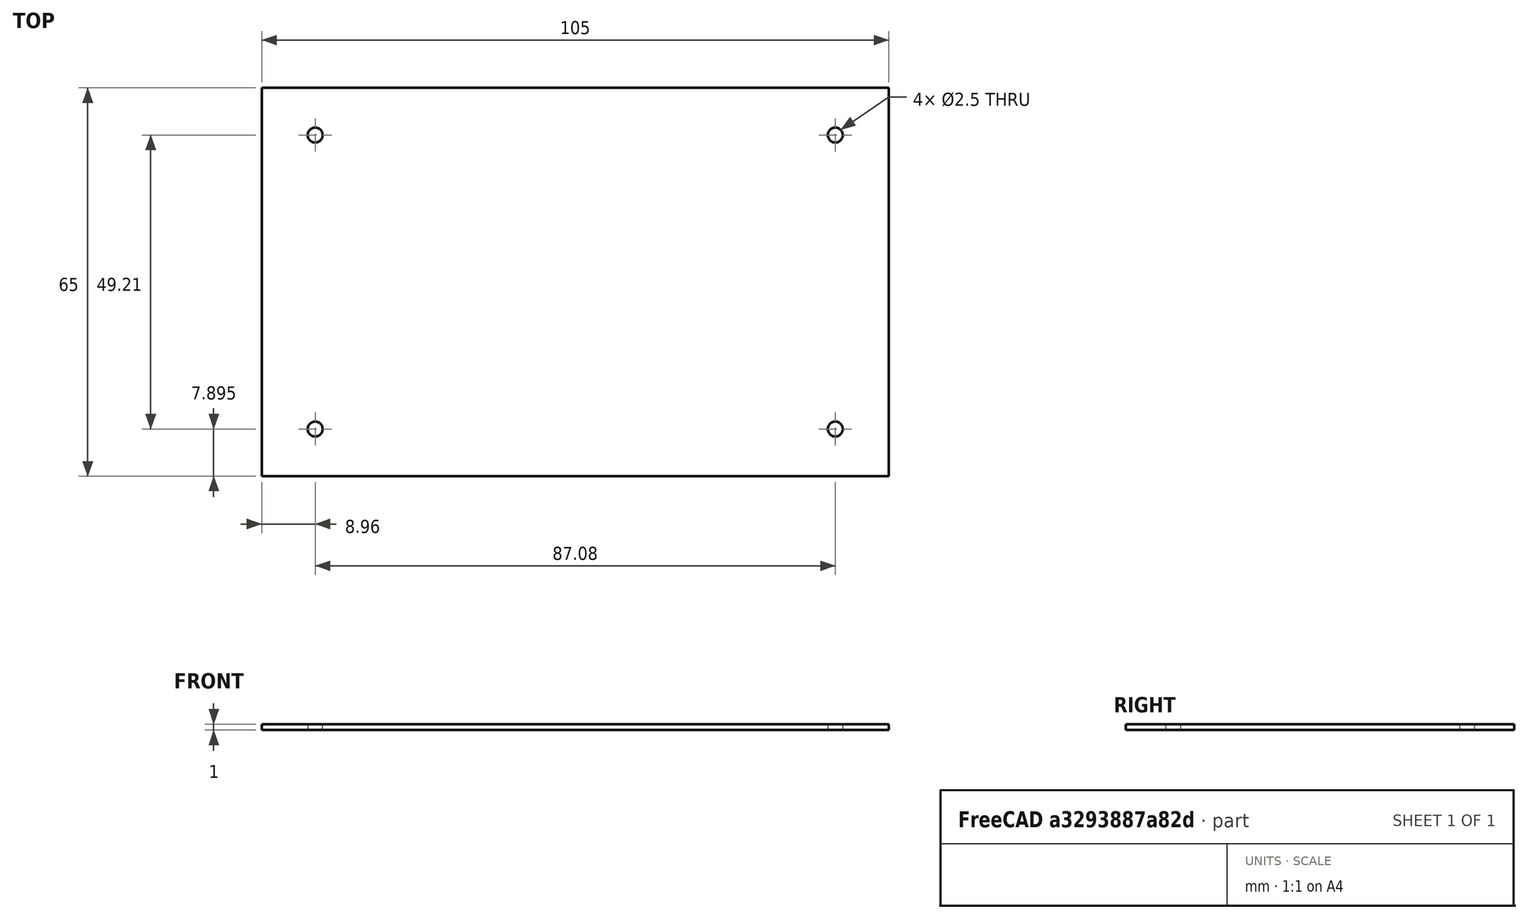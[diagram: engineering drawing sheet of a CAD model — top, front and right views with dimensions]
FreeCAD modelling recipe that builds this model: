
FCSTD DOCUMENT  (FreeCAD 1.0R39319 (Git))
Label: camera-holder
License: All rights reserved
LicenseURL: https://en.wikipedia.org/wiki/All_rights_reserved
objects: Sketcher::SketchObject×2, App::VarSet×1, PartDesign::Pad×1, PartDesign::Body×1
note: 8 computed .brp shape members not serialized (recipe doc carries the construction recipe); baked Part::Feature solids carry a one-line shape summary decoded from their .brp

FEATURE [Sketcher::SketchObject] Sketch
  ArcFitTolerance = 1e-06
  AttachmentSupport = -> [XY_Plane]
  FullyConstrained = true
  MakeInternals = false
  MapMode = 5
  expr: Constraints[10] = <<Case_Dimensions>>.screw_diameter
  expr: Constraints[14] = <<Case_Dimensions>>.length_screw_offset
  expr: Constraints[15] = <<Case_Dimensions>>.width_screw_offset
  expr: Constraints[17] = (<<Case_Dimensions>>.length - <<Case_Dimensions>>.length_screw_offset) / 2
  expr: Constraints[18] = (<<Case_Dimensions>>.width - <<Case_Dimensions>>.width_screw_offset) / 2
  expr: Constraints[19] = <<Case_Dimensions>>.width / 2
  expr: Constraints[20] = <<Case_Dimensions>>.length / 2
  expr: Constraints[21] = <<Case_Dimensions>>.screw_diameter
  expr: Constraints[22] = <<Case_Dimensions>>.screw_diameter
  expr: Constraints[23] = <<Case_Dimensions>>.screw_diameter
  expr: Constraints[8] = <<Case_Dimensions>>.length
  expr: Constraints[9] = <<Case_Dimensions>>.width
  sketch-geometry (8):
    g0: LineSegment StartX=-52.5 StartY=32.5 StartZ=0 EndX=-52.5 EndY=-32.5 EndZ=0
    g1: LineSegment StartX=-52.5 StartY=-32.5 StartZ=0 EndX=52.5 EndY=-32.5 EndZ=0
    g2: LineSegment StartX=52.5 StartY=-32.5 StartZ=0 EndX=52.5 EndY=32.5 EndZ=0
    g3: LineSegment StartX=-52.5 StartY=32.5 StartZ=0 EndX=52.5 EndY=32.5 EndZ=0
    g4: Circle CenterX=43.54 CenterY=24.605 CenterZ=0 NormalX=0 NormalY=0 NormalZ=1 AngleXU=0 Radius=1.25
    g5: Circle CenterX=-43.54 CenterY=24.605 CenterZ=0 NormalX=0 NormalY=0 NormalZ=1 AngleXU=0 Radius=1.25
    g6: Circle CenterX=-43.54 CenterY=-24.605 CenterZ=0 NormalX=0 NormalY=0 NormalZ=1 AngleXU=0 Radius=1.25
    g7: Circle CenterX=43.54 CenterY=-24.605 CenterZ=0 NormalX=0 NormalY=0 NormalZ=1 AngleXU=0 Radius=1.25
  constraints (24):
    c: Vertical(g0)
    c: Coincident(g1,g0)
    c: Horizontal(g1)
    c: Coincident(g2,g1)
    c: Coincident(g3,g0)
    c: Coincident(g3,g2)
    c: Vertical(g2,g1)
    c: Horizontal(g0,g2)
    c: DistanceX(g3,g3) = 105
    c: DistanceY(g2,g2) = 65
    c: Diameter(g7) = 2.5
    c: Vertical(g5,g6)
    c: Horizontal(g5,g4)
    c: Vertical(g7,g4)
    c: DistanceX(g5,g4) = 87.08
    c: DistanceY(g7,g4) = 49.21
    c: Horizontal(g7,g6)
    c: Distance(g5,g0) = 8.96
    c: Distance(g5,g3) = 7.895
    c: Distance(g-1,g3) = 32.5
    c: Distance(g2,g-2) = 52.5
    c: Diameter(g6) = 2.5
    c: Diameter(g4) = 2.5
    c: Diameter(g5) = 2.5
FEATURE [App::VarSet] VarSet  label="Case_Dimensions"
  height = 41.5
  length = 105
  length_screw_offset = 87.08
  screw_diameter = 2.5
  thickness = 1
  vent_hole_height = 36.5
  vent_hole_width = 5
  width = 65
  width_screw_offset = 49.21
  expr: height = thickness + 40.5 mm
  expr: vent_hole_height = height - 5 mm
FEATURE [PartDesign::Pad] Pad
  Direction = (0,0,1)
  Length = 1
  Length2 = 10
  Profile = -> Sketch
  ReferenceAxis = -> Sketch [N_Axis]
  Refine = true
  Suppressed = false
  Type = 0
  expr: Length = <<Case_Dimensions>>.thickness
FEATURE [PartDesign::Body] Body
  AllowCompound = false
  Group = -> [Sketch,Pad]
  Origin = -> Origin
  Tip = -> Pad
FEATURE [Sketcher::SketchObject] Sketch001
  ArcFitTolerance = 1e-06
  AttachmentSupport = -> [Pad]
  ExternalGeometry = -> [Pad]
  FullyConstrained = false
  MakeInternals = false
  MapMode = 5
  Placement = pos=(0,-32.5,0) rot=(1,0,0;1.5708rad)
  expr: Constraints[10] = <<Case_Dimensions>>.height
  expr: Constraints[19] = <<Case_Dimensions>>.vent_hole_width
  expr: Constraints[20] = <<Case_Dimensions>>.vent_hole_height
  expr: Constraints[21] = (<<Case_Dimensions>>.height - <<Case_Dimensions>>.vent_hole_height) / 2
  sketch-geometry (8):
    g0: LineSegment StartX=-52.5 StartY=0 StartZ=0 EndX=52.5 EndY=0 EndZ=0
    g1: LineSegment StartX=52.5 StartY=0 StartZ=0 EndX=52.5 EndY=41.5 EndZ=0
    g2: LineSegment StartX=52.5 StartY=41.5 StartZ=0 EndX=-52.5 EndY=41.5 EndZ=0
    g3: LineSegment StartX=-52.5 StartY=41.5 StartZ=0 EndX=-52.5 EndY=0 EndZ=0
    g4: LineSegment StartX=-42.3937 StartY=39 StartZ=0 EndX=-42.3937 EndY=2.5 EndZ=0
    g5: LineSegment StartX=-42.3937 StartY=2.5 StartZ=0 EndX=-37.3937 EndY=2.5 EndZ=0
    g6: LineSegment StartX=-37.3937 StartY=2.5 StartZ=0 EndX=-37.3937 EndY=39 EndZ=0
    g7: LineSegment StartX=-37.3937 StartY=39 StartZ=0 EndX=-42.3937 EndY=39 EndZ=0
  constraints (22):
    c: Coincident(g0,g1)
    c: Coincident(g1,g2)
    c: Coincident(g2,g3)
    c: Coincident(g3,g0)
    c: Horizontal(g0)
    c: Horizontal(g2)
    c: Vertical(g1)
    c: Vertical(g3)
    c: Coincident(g0,g-3)
    c: Equal(g0,g-3)
    c: DistanceY(g1,g1) = 41.5
    c: Coincident(g4,g5)
    c: Coincident(g5,g6)
    c: Coincident(g6,g7)
    c: Coincident(g7,g4)
    c: Vertical(g4)
    c: Vertical(g6)
    c: Horizontal(g5)
    c: Horizontal(g7)
    c: DistanceX(g7,g7) = 5
    c: DistanceY(g6,g6) = 36.5
    c: Distance(g2,g7) = 2.5
